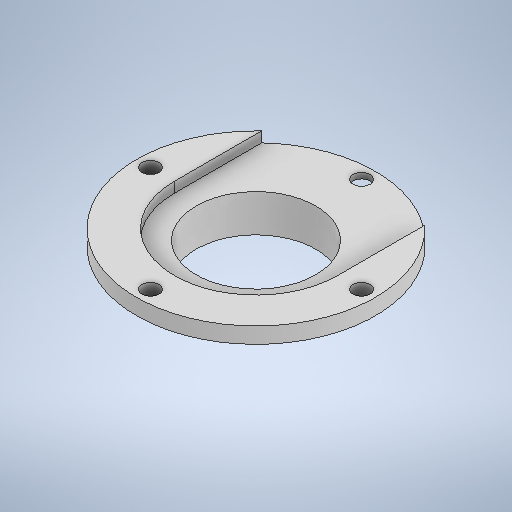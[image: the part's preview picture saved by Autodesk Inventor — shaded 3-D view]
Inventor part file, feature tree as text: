
AUTODESK INVENTOR PART (.ipt)
format: ipt  version: 2025.2 (Build 292293000, 293)  size: 271,360 bytes
history: native  units: mm
features: sketch x5, extrude x4
ambient origin geometry x8: Origin, YZ Plane, XZ Plane, XY Plane, X Axis, Y Axis, Z Axis, Center Point
bodies: Solid1 (feature_tree)
feature tree (9):
  extrude  "Extrusion1"  Depth=45.0mm
  extrude  "Extrusion2"  Depth=4.3mm
  extrude  "Extrusion3"  Depth=4.0mm TaperAngle=0.0deg
  extrude  "Extrusion4"  Depth=2.6mm TaperAngle=0.0deg
  sketch  "Sketch1"  dims[d0=60.0mm d1=45.0mm]
  sketch  "Sketch Circular Pattern1"  dims[d3=53.0mm d4=4.3mm]
  sketch  "Sketch2"  dims[d5=40.0mm d7=360.0deg d9=4.0mm d10=0.0mm]
  sketch  "Sketch3"  dims[d11=41.0mm d12=2.6mm d13=0.0mm]
  sketch  "Sketch4"  dims[d14=30.0mm d15=0.0mm d16=0.0mm d17=30.0mm d18=35.0mm d19=8.0mm d20=0.0mm]
